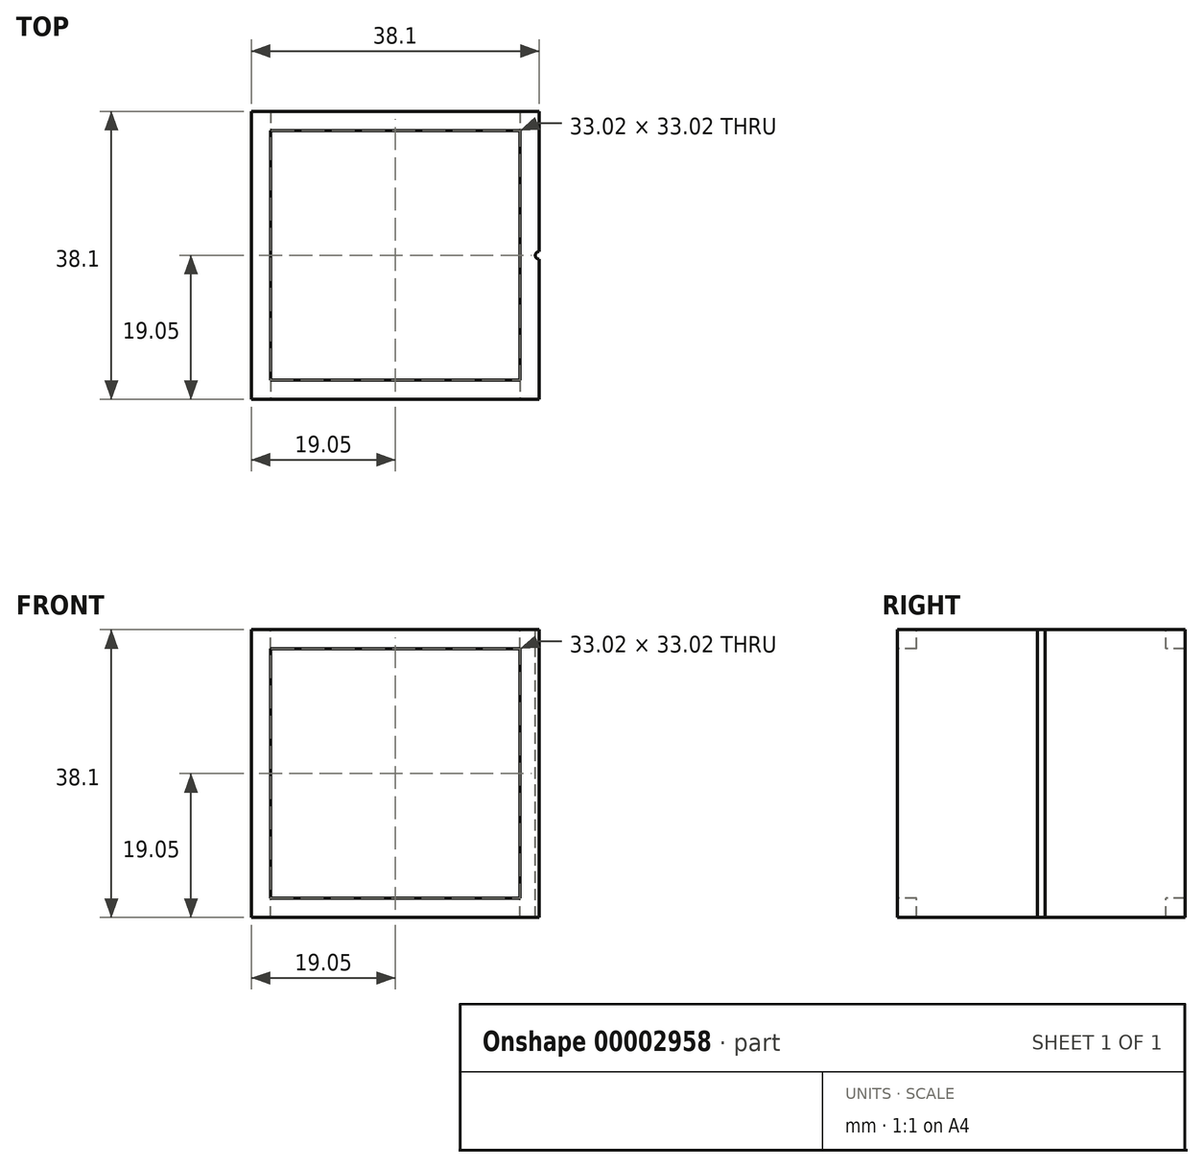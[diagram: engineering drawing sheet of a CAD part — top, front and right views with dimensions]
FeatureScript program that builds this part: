
annotation { "Feature Type Name" : "Feature", "Feature Type Description" : "" }
export const myFeature = defineFeature(function(context is Context, id is Id, definition is map)
    precondition{}
    {
        {
            var Q0;
            Q0=qCreatedBy(makeId("Front.planeOp"),FACE);
            var sketch = newSketch(context, id + "F0", { "sketchPlane" : qUnion([Q0])});
            skLineSegment(sketch, "E0.rect.bottom", {"start": v(-19.05, -19.05) * mm, "end": v(19.05, -19.05) * mm});
            skLineSegment(sketch, "E0.rect.top", {"start": v(-19.05, 19.05) * mm, "end": v(19.05, 19.05) * mm});
            skLineSegment(sketch, "E0.rect.left", {"start": v(-19.05, -19.05) * mm, "end": v(-19.05, 19.05) * mm});
            skLineSegment(sketch, "E0.rect.right", {"start": v(19.05, -19.05) * mm, "end": v(19.05, 19.05) * mm});
            skPoint(sketch, "E0.rect.middle", {"position": v(0, 0) * mm});
            skSolve(sketch);
        }
        {
            var Q0;
            Q0=makeQuery(id+"F0.imprint","IMPRINT",FACE,{"disambiguationData":[TD([[makeQuery(id+"F0.imprint","IMPRINT",EDGE,{"derivedFrom":sQuery(id+"F0.wireOp",EDGE,"E0.rect.bottom")}),1.0]])]});
            extrude(context, id + "F1", {"entities" : qUnion([Q0]), "depth" : 38.1 * mm});
        }
        {
            var Q0;
            Q0=makeQuery(id+"F1.opExtrude","SWEPT_FACE",FACE,{"disambiguationData":[OSD([sQuery(id+"F0.wireOp",EDGE,"E0.rect.top")])]});
            var sketch = newSketch(context, id + "F2", { "sketchPlane" : qUnion([Q0])});
            skLineSegment(sketch, "E1.0", {"start": v(-16.51, -35.56) * mm, "end": v(-16.51, -2.54) * mm});
            skLineSegment(sketch, "E1.1", {"start": v(-16.51, -35.56) * mm, "end": v(16.5, -35.56) * mm});
            skLineSegment(sketch, "E1.2", {"start": v(16.5, -35.56) * mm, "end": v(16.5, -2.54) * mm});
            skLineSegment(sketch, "E1.3", {"start": v(-16.51, -2.54) * mm, "end": v(16.5, -2.54) * mm});
            skSolve(sketch);
        }
        {
            var Q0;
            Q0=makeQuery(id+"F2.imprint","IMPRINT",FACE,{"disambiguationData":[TD([[makeQuery(id+"F2.imprint","IMPRINT",EDGE,{"derivedFrom":sQuery(id+"F2.wireOp",EDGE,"E1.0")}),-1.0]])]});
            extrude(context, id + "F3", {"entities" : qUnion([Q0]), "operationType" : NewBodyOperationType.REMOVE, "endBound" : BoundingType.THROUGH_ALL, "oppositeDirection" : true, "depth" : 25.4 * mm});
        }
        {
            var Q0;
            Q0=makeQuery(id+"F1.opExtrude","CAP_FACE",FACE,{"disambiguationData":[OSD([sQuery(id+"F0.wireOp",EDGE,"E0.rect.bottom"),sQuery(id+"F0.wireOp",EDGE,"E0.rect.top"),sQuery(id+"F0.wireOp",EDGE,"E0.rect.left"),sQuery(id+"F0.wireOp",EDGE,"E0.rect.right")])],"isStart":false});
            var sketch = newSketch(context, id + "F4", { "sketchPlane" : qUnion([Q0])});
            skLineSegment(sketch, "E2.0", {"start": v(-16.51, 16.51) * mm, "end": v(16.5, 16.51) * mm});
            skLineSegment(sketch, "E2.1", {"start": v(-16.5, -16.51) * mm, "end": v(-16.51, 16.51) * mm});
            skLineSegment(sketch, "E2.2", {"start": v(-16.5, -16.51) * mm, "end": v(16.51, -16.51) * mm});
            skLineSegment(sketch, "E2.3", {"start": v(16.51, -16.51) * mm, "end": v(16.5, 16.51) * mm});
            skSolve(sketch);
        }
        {
            var Q0;
            Q0=makeQuery(id+"F4.imprint","IMPRINT",FACE,{"disambiguationData":[TD([[makeQuery(id+"F4.imprint","IMPRINT",EDGE,{"derivedFrom":sQuery(id+"F4.wireOp",EDGE,"E2.0")}),-1.0]])]});
            extrude(context, id + "F5", {"entities" : qUnion([Q0]), "operationType" : NewBodyOperationType.REMOVE, "endBound" : BoundingType.THROUGH_ALL, "oppositeDirection" : true, "depth" : 25.4 * mm});
        }
        {
            var Q0;
            Q0=makeQuery(id+"F1.opExtrude","SWEPT_FACE",FACE,{"disambiguationData":[OSD([sQuery(id+"F0.wireOp",EDGE,"E0.rect.top")])]});
            var sketch = newSketch(context, id + "F6", { "sketchPlane" : qUnion([Q0])});
            skArc(sketch, "E3", {"start": v(19.05, -18.54) * mm, "mid": v(18.54, -19.05) * mm, "end": v(19.05, -19.56) * mm});
            skPoint(sketch, "E4", {"position": v(19.05, -18.54) * mm});
            skPoint(sketch, "E5", {"position": v(19.05, -19.56) * mm});
            skSolve(sketch);
        }
        {
            var Q0;
            {var subQ1=sQuery(id+"F6.wireOp",EDGE,"E3");Q0=makeQuery(id+"F6.imprint","IMPRINT",FACE,{"disambiguationData":[TD([[makeQuery(id+"F6.imprint","IMPRINT",EDGE,{"derivedFrom":subQ1}),1.0]])]});}
            extrude(context, id + "F7", {"entities" : qUnion([Q0]), "operationType" : NewBodyOperationType.REMOVE, "endBound" : BoundingType.THROUGH_ALL, "oppositeDirection" : true, "depth" : 25.4 * mm});
        }
    });
